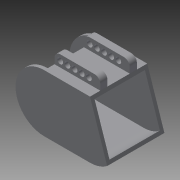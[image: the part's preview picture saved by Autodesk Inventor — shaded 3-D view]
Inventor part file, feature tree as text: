
AUTODESK INVENTOR PART (.ipt)
format: ipt  version: 2015 (Build 190159000, 159)  size: 187,392 bytes
history: native  units: in
note: dims shown in document units (in); Inventor stores cm internally (conversion verified against a paired STEP export)
features: extrude x7, sketch x7, projected_geometry x5, plane x2
ambient origin geometry x8: Origin, YZ Plane, XZ Plane, XY Plane, X Axis, Y Axis, Z Axis, Center Point
bodies: Solid1 (feature_tree)
feature tree (21):
  extrude  "Extrusion1"  Depth=2.5in TaperAngle=0.0deg
  plane  "Work Plane1"
  extrude  "Extrusion2"  Depth=2.2in TaperAngle=0.0deg
  extrude  "Extrusion3"  Depth=2.5in TaperAngle=0.0deg
  extrude  "Extrusion4"  Depth=1.25in
  extrude  "Extrusion5"  Depth=0.3125in
  extrude  "Extrusion6"  Depth=0.5in TaperAngle=0.0deg
  plane  "Work Plane2"
  extrude  "Extrusion7"  Depth=0.3125in
  sketch  "Sketch1"  dims[d0=2.5in d2=2.5in d3=0.0in]
  sketch  "Sketch2"  dims[d4=-1.25in d5=2.2in d6=0.0in]
  projected_geometry  "Projected Loop1"
  sketch  "Sketch3"  dims[d7=2.5in d8=2.5in d9=0.0in]
  sketch  "Sketch4"  dims[d10=1.25in d11=0.8in]
  projected_geometry  "Projected Loop2"
  sketch  "Sketch5"  dims[d12=1.6in d13=0.3125in]
  projected_geometry  "Projected Loop3"
  sketch  "Sketch6"  dims[d14=0.3125in d15=0.5in d16=0.0in]
  projected_geometry  "Projected Loop4"
  sketch  "Sketch8"  dims[d17=2.5in d18=0.0in d20=1.9685in d22=0.3125in d23=0.3937in d25=1.0in d27=2.5in d28=0.0in d29=1.25in d30=0.0in d31=0.25in]
  projected_geometry  "Projected Loop6"
